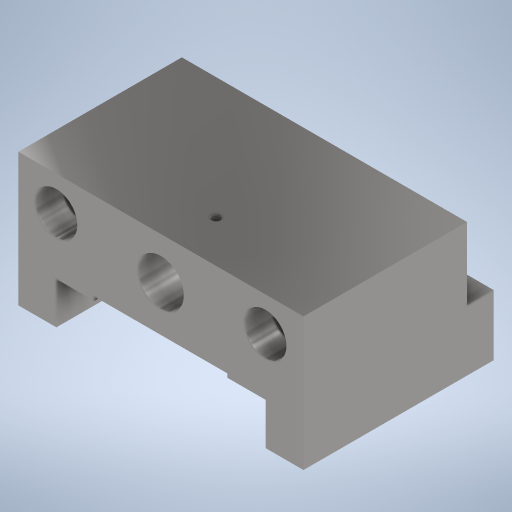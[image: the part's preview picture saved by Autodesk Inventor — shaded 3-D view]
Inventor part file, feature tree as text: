
AUTODESK INVENTOR PART (.ipt)
format: ipt  version: 2023.2 (Build 272271000, 271)  size: 304,640 bytes
history: native  units: mm
features: sketch x6, hole x4, extrude x2
ambient origin geometry x8: Origin, YZ Plane, XZ Plane, XY Plane, X Axis, Y Axis, Z Axis, Center Point
bodies: Solid1 (feature_tree)
feature tree (12):
  extrude  "Extrusion1"  Depth=35.0mm
  extrude  "Extrusion2"  Depth=11.0mm
  hole  "Hole1"  [1 undecoded]
  hole  "Hole2"  [1 undecoded]
  hole  "Hole3"  [1 undecoded]
  hole  "Hole4"  [1 undecoded]
  sketch  "Sketch1"  dims[d0=75.0mm d1=35.0mm]
  sketch  "Sketch2"  dims[d2=10.0mm d3=11.0mm]
  sketch  "Sketch3"  dims[d4=10.0mm d5=90.0deg]
  sketch  "Sketch4"  dims[d6=1.0mm d7=35.0mm]
  sketch  "Sketch5"  dims[d8=10.0mm d9=11.0mm]
  sketch  "Sketch6"  dims[d10=50.0mm d11=0.0mm d12=7.0mm d13=19.0mm d14=0.0mm d15=0.0mm d16=26.0mm d17=26.0mm d18=10.0mm d19=10.0mm d20=6.4mm d21=0.5mm d22=11.0mm d23=7.0mm d24=90.0deg d25=8.0mm d26=20.594885mm d27=24.0mm d28=37.5mm d29=12.0mm d30=6.0mm d31=12.0mm d32=6.0mm d33=90.0deg d34=20.0mm d35=0.0mm d36=34.0mm d37=2.459mm d38=6.0mm d39=4.0mm d40=2.0mm d41=90.0deg d42=8.8mm d43=0.0mm d44=11.0mm d45=5.0mm d46=5.0mm d47=5.0mm d48=5.0mm d50=7.0mm d51=7.0mm d52=7.0mm d53=4.134mm d54=5.0mm d55=4.0mm d56=2.0mm d57=90.0deg d58=14.2mm d59=0.0mm d60=36.0mm]
note: 4 required parameter values undecoded (feature->parameter linkage not recoverable at this tier; creation-order binding heuristic only, values carry confidence <= 0.55)
